# Revit family: Shower_Freestanding_Nero_Zen
name_source: partatom
category: Plumbing Fixtures
units: mm (PartAtom-declared; Revit-internal decimal feet)

## family parameters
Always vertical = Yes
Cut with Voids When Loaded = Yes
Maintain Annotation Orientation = No
OmniClass Number = 23.31.17.00
OmniClass Title = Showers
Part Type = Normal
Room Calculation Point = No
Round Connector Dimension = Use Diameter
Shared = No
Work Plane-Based = No

## types (4) — shared parameters
Assembly Code = D2010710
CW Connection = Yes
HW Connection = Yes
HoseMaterial = Metal_MatteBlack_Nero
IfcExportAs = IfcSanitaryTerminal
IfcExportType = SHOWER
Manufacturer = Nero
ManufacturerOverallDepth = 629.5 mm
ManufacturerOverallHeight = 2096 mm
ManufacturerOverallWidth = 300 mm
ManufacturerURLProductSpecific = https://nerotapware.com.au
ModifiedIssue = 20240705 $
URL = https://nerotapware.com.au
Uniclass2015Code = Pr_40_20_87_75
Uniclass2015Title = Shower fittings package
Uniclass2015Version = Products v1.28
Vent Connection = No
Waste Connection = No
zero-valued in all types: Default Elevation

## per-type parameters (varying)
| type | BodyMaterial | Description | ManufacturerSpecCode | Model | Type Comments |
| Graphite (NR162205aGR) | Metal_Graphite_Nero_Brushed | Zen SS316L Outdoor Freestanding Shower Column Graphite | NR162205aGR | NR162205aGR | Shower - SS316L - Freestanding - Graphite |
| Brushed Bronze (NR162205aBZ) | Metal_Bronze_Nero_Brushed | Zen SS316L Outdoor Freestanding Shower Column Brushed Bronze | NR162205aBZ | NR162205aBZ | Shower - SS316L - Freestanding - Brushed Bronze |
| Brushed Gold (NR162205aBG) | Metal_Gold_Nero_Brushed | Zen SS316L Outdoor Freestanding Shower Column Brushed Gold | NR162205aBG | NR162205aBG | Shower - SS316L - Freestanding - Brushed Gold |
| Brushed Nickel (NR162205aBN) | Metal_Nickel_Nero_Brushed | Zen SS316L Outdoor Freestanding Shower Column Brushed Nickel | NR162205aBN | NR162205aBN | Shower - SS316L - Freestanding - Brushed Nickel |

## geometry (parser evidence)
native form markers: Sweep x2
no freeform markers — native parametric forms only
